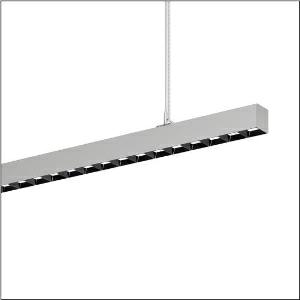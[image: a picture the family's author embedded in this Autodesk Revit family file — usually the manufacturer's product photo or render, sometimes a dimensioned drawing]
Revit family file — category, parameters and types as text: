
# Revit family: silica_21_51mx34dc3dsb
name_source: partatom
category: Lighting Fixtures
units: mm (PartAtom-declared; Revit-internal decimal feet)

## family parameters
Cut with Voids When Loaded = No
Host = Face
Light Source = No
Part Type = Normal
Room Calculation Point = No
Round Connector Dimension = Use Diameter
Shared = No

## types (1)
- --- (1 x LED, 19200 lm, 129.1 W, 3000K)
    Apparent Load = 129 VA
    CIE Flux Codes = 74 94 99 56 100
    Color Rendering = 80
    Color Temperature = 3000K
    Default Elevation = 1800 mm
    Description = Silica 21, office luminaire, primary light control with darklight reflector, of PMMA, black, light emission: direct/indirect distribution, primary light characteristic: asymmetric, installation type: suspended mounting, LED, rated luminous flux: 19.200lm, luminous efficacy: 149lm/W, light colour: 830, colour temperature: 3000K, control gear: DALI 2, with terminal, 3+2-pole, max. 2.5mm², mains connection: 220..240V, AC, 50/60Hz, rated input power: 129.1W, luminaire housing, of aluminium, metallic grey (RAL 9006), length: 3.004mm, width: 53mm, height: 53mm, protection rating (complete): IP20, insulation class (complete): insulation class I (protective earthing), certification: CE, permissible operating ambient temperature: 0..+35°C, standard: EN 50419, packaging unit: 1 piece
    Height = 53 mm
    Lamp = 1 x LED
    Lamp Light Flux = 19200 lm
    Lamp Power = 129.1 W
    Lamp count = 1
    Length = 3004 mm
    Luminous efficacy = 149 lm/W
    Manufacturer = Siteco
    ModVariant = No
    Model = 51MX34DC3DSB
    Mounting Place = Ceiling
    Mounting Type = Pendant
    Number of Poles = 1
    OnlyDefault = Yes
    Power Factor = 1
    Product Name = Silica 21
    Product group = office luminaire | ceiling pendant
    ProductGroupID = 903
    Protection Class = Protection class I
    Protection Degree = IP 20
    RLX_Detail_Level = 1
    RLX_Emergency_Light_Flux = 0 lm
    RLX_Emergency_Type = 0
    RLX_Emergency_Type_DB = No
    RlxData = <blob elided: 68129 chars, md5=331f5133>
    Socket = socket
    Standby Power = 0 W
    System Light Flux = 19200 lm
    System Power = 129 W
    Type Comments = factory setting: luminous flux: 100 % | dim-lin: 254 | 448 mA
    Type Image = l_1335859.jpg
    URL = http://relux.com
    VarID = @adj_121565
    Voltage = 0 V
    Weight = 0.00 kg
    Width = 53 mm

## geometry (parser evidence)
native form markers: Blend x4, Sweep x11
no freeform markers — native parametric forms only
